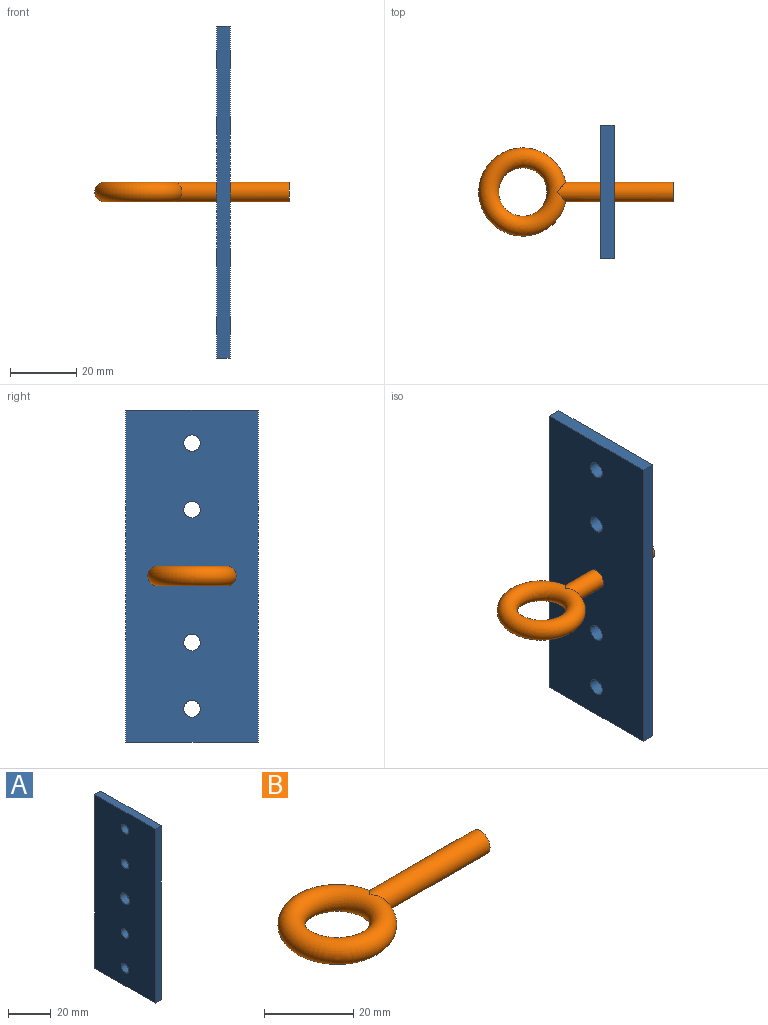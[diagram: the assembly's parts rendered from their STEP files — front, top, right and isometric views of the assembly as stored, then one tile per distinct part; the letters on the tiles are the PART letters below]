
ASSEMBLY  parts=2 mates=1
PART A: 11 faces, bbox 4x40x100 mm
  f0: plane 100x4mm, normal (0,-1,0), area 400mm2, adj f1,f7,f9,f10
  f1: plane 40x4mm, normal (0,0,-1), area 160mm2, adj f0,f2,f9,f10
  f2: plane 100x4mm, normal (0,1,0), area 400mm2, adj f1,f7,f9,f10
  f3: cylinder r=2.5mm len=5mm, axis (-1,0,0), area 62.8mm2, adj f9,f10
  f4: cylinder r=2.5mm len=5mm, axis (-1,0,0), area 62.8mm2, adj f9,f10
  f5: cylinder r=2.5mm len=5mm, axis (-1,0,0), area 62.8mm2, adj f9,f10
  f6: cylinder r=3mm len=6mm, axis (-1,0,0), area 75.4mm2, adj f9,f10
  f7: plane 40x4mm, normal (0,0,1), area 160mm2, adj f0,f2,f9,f10
  f8: cylinder r=2.5mm len=5mm, axis (-1,0,0), area 62.8mm2, adj f9,f10
  f9: plane 100x40mm, normal (1,0,0), area 3893.2mm2, adj f0,f1,f2,f3,f4,f5,f6,f7
  f10: plane 100x40mm, normal (-1,0,0), area 3893.2mm2, adj f0,f1,f2,f3,f4,f5,f6,f7
PART B: 3 faces, bbox 59.7x28.7x6 mm
  f0: cylinder r=3mm len=35mm, axis (-1,0,0), area 627.3mm2, adj f1,f2
  f1: plane 6x6mm, normal (1,0,0), area 28.3mm2, adj f0
  f2: torus R=10.28mm, axis (0,0,1), area 1181.3mm2, adj f0
PLACE A t=(24.97,5.54,-50.48)mm
PLACE B t=(1.5,25.54,-0.48)mm
MATE slider B.f0 <-> A.f6  axis (1,0,0) through (46.8,25.54,-0.48)mm
